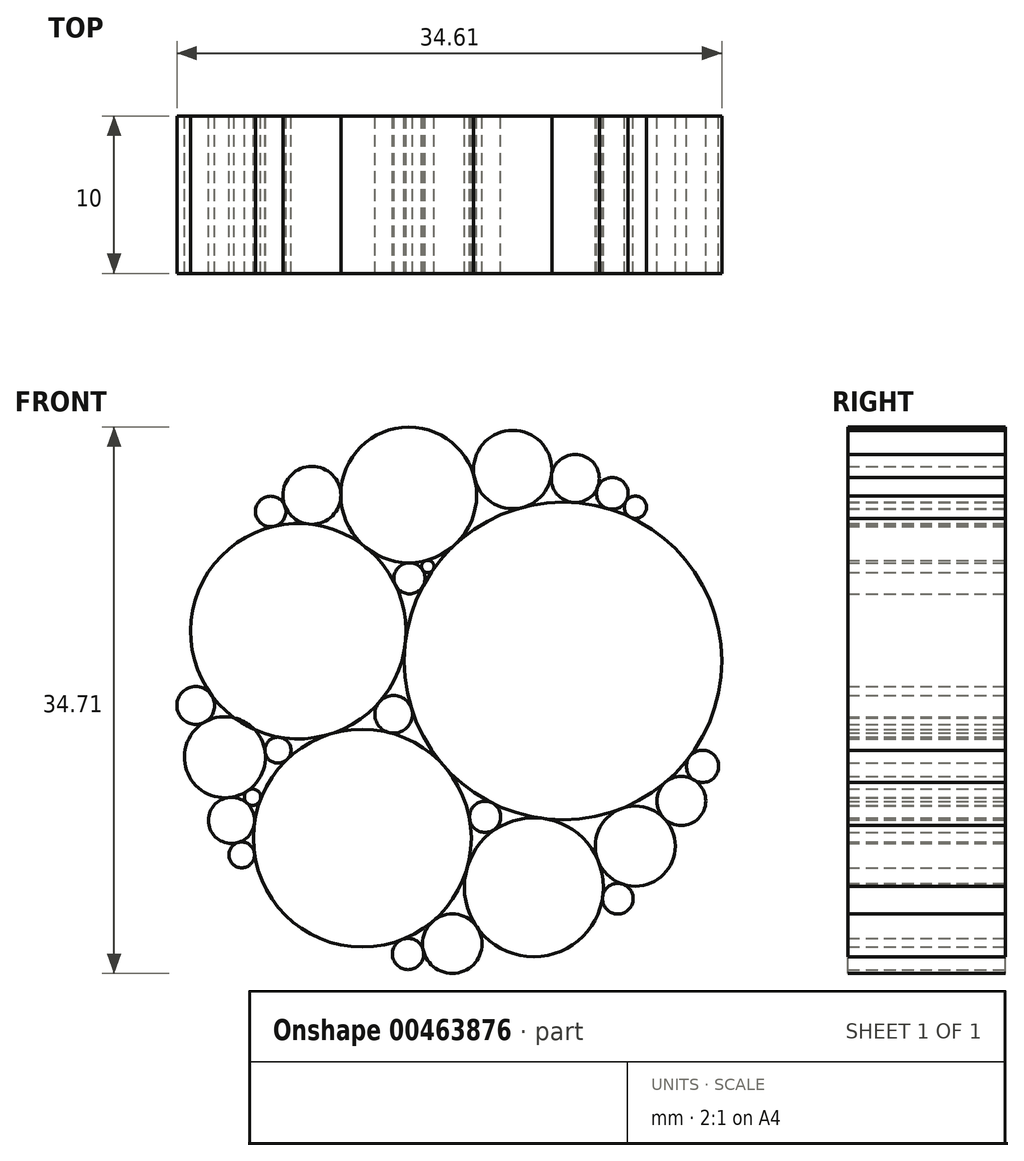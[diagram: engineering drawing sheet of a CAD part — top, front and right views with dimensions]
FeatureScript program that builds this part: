
annotation { "Feature Type Name" : "Feature", "Feature Type Description" : "" }
export const myFeature = defineFeature(function(context is Context, id is Id, definition is map)
    precondition{}
    {
        {
            var Q0;
            Q0=qCreatedBy(makeId("Front.planeOp"),FACE);
            var sketch = newSketch(context, id + "F0", { "sketchPlane" : qUnion([Q0])});
            skCircle(sketch, "E0", {"center": v(0, 0) * mm, "radius": 17.5 * mm});
            skCircle(sketch, "E1", {"center": v(-2.77, 12.9) * mm, "radius": 4.31 * mm});
            skPoint(sketch, "E1.first.point", {"position": v(-3.67, 17.11) * mm});
            skPoint(sketch, "E1.second.point", {"position": v(-3.67, 17.11) * mm});
            skPoint(sketch, "E1.third.point", {"position": v(-2.48, 8.6) * mm});
            skCircle(sketch, "E2", {"center": v(-5.71, -8.9) * mm, "radius": 6.92 * mm});
            skPoint(sketch, "E2.first.point", {"position": v(-9.45, -14.73) * mm});
            skPoint(sketch, "E2.second.point", {"position": v(-9.45, -14.73) * mm});
            skPoint(sketch, "E2.third.point", {"position": v(-1.47, -3.44) * mm});
            skCircle(sketch, "E3", {"center": v(-8.92, 12.87) * mm, "radius": 1.84 * mm});
            skPoint(sketch, "E3.first.point", {"position": v(-9.97, 14.38) * mm});
            skPoint(sketch, "E3.second.point", {"position": v(-9.97, 14.38) * mm});
            skPoint(sketch, "E3.third.point", {"position": v(-7.42, 11.8) * mm});
            skCircle(sketch, "E4", {"center": v(-1.56, 8.35) * mm, "radius": 0.4 * mm});
            skPoint(sketch, "E4.first.point", {"position": v(-1.66, 8.73) * mm});
            skPoint(sketch, "E4.second.point", {"position": v(-1.66, 8.73) * mm});
            skPoint(sketch, "E4.third.point", {"position": v(-1.33, 8.03) * mm});
            skCircle(sketch, "E5", {"center": v(3.84, 14.51) * mm, "radius": 2.49 * mm});
            skPoint(sketch, "E5.first.point", {"position": v(1.42, 13.92) * mm});
            skPoint(sketch, "E5.second.point", {"position": v(4.47, 16.92) * mm});
            skPoint(sketch, "E5.third.point", {"position": v(5.7, 12.86) * mm});
            skCircle(sketch, "E6", {"center": v(0, -15.61) * mm, "radius": 1.89 * mm});
            skPoint(sketch, "E6.first.point", {"position": v(0, -17.5) * mm});
            skPoint(sketch, "E6.second.point", {"position": v(0, -17.5) * mm});
            skPoint(sketch, "E6.third.point", {"position": v(-0.04, -13.72) * mm});
            skCircle(sketch, "E7", {"center": v(-9.79, 4.24) * mm, "radius": 6.84 * mm});
            skPoint(sketch, "E7.first.point", {"position": v(-16.06, 6.95) * mm});
            skPoint(sketch, "E7.second.point", {"position": v(-16.06, 6.95) * mm});
            skPoint(sketch, "E7.third.point", {"position": v(-2.95, 4.31) * mm});
            skCircle(sketch, "E8", {"center": v(-14.45, -3.77) * mm, "radius": 2.57 * mm});
            skPoint(sketch, "E8.first.point", {"position": v(-16.93, -4.41) * mm});
            skPoint(sketch, "E8.second.point", {"position": v(-16.93, -4.41) * mm});
            skPoint(sketch, "E8.third.point", {"position": v(-13.85, -1.26) * mm});
            skCircle(sketch, "E9", {"center": v(-14.02, -7.78) * mm, "radius": 1.46 * mm});
            skPoint(sketch, "E9.first.point", {"position": v(-15.3, -8.5) * mm});
            skPoint(sketch, "E9.second.point", {"position": v(-15.3, -8.5) * mm});
            skPoint(sketch, "E9.third.point", {"position": v(-12.57, -7.98) * mm});
            skCircle(sketch, "E10", {"center": v(-2.72, 7.6) * mm, "radius": 0.99 * mm});
            skPoint(sketch, "E10.first.point", {"position": v(-3.61, 7.17) * mm});
            skPoint(sketch, "E10.second.point", {"position": v(-2.73, 8.59) * mm});
            skPoint(sketch, "E10.third.point", {"position": v(-1.85, 7.13) * mm});
            skCircle(sketch, "E11", {"center": v(-3.73, -1.04) * mm, "radius": 1.2 * mm});
            skPoint(sketch, "E11.first.point", {"position": v(-4.63, -0.25) * mm});
            skPoint(sketch, "E11.second.point", {"position": v(-4.02, -2.2) * mm});
            skPoint(sketch, "E11.third.point", {"position": v(-2.56, -1.3) * mm});
            skCircle(sketch, "E12", {"center": v(-11.53, 11.84) * mm, "radius": 0.97 * mm});
            skPoint(sketch, "E12.first.point", {"position": v(-12.2, 12.54) * mm});
            skPoint(sketch, "E12.second.point", {"position": v(-12.2, 12.54) * mm});
            skPoint(sketch, "E12.third.point", {"position": v(-11.32, 10.9) * mm});
            skCircle(sketch, "E13", {"center": v(-11.08, -3.32) * mm, "radius": 0.83 * mm});
            skPoint(sketch, "E13.first.point", {"position": v(-11.9, -3.43) * mm});
            skPoint(sketch, "E13.second.point", {"position": v(-10.94, -2.5) * mm});
            skPoint(sketch, "E13.third.point", {"position": v(-10.5, -3.91) * mm});
            skCircle(sketch, "E14", {"center": v(7.03, 2.35) * mm, "radius": 10.09 * mm});
            skPoint(sketch, "E14.first.point", {"position": v(16.6, 5.55) * mm});
            skPoint(sketch, "E14.second.point", {"position": v(16.6, 5.55) * mm});
            skCircle(sketch, "E15", {"center": v(2.08, -7.55) * mm, "radius": 0.99 * mm});
            skPoint(sketch, "E15.first.point", {"position": v(1.1, -7.72) * mm});
            skPoint(sketch, "E15.second.point", {"position": v(2.52, -6.67) * mm});
            skPoint(sketch, "E15.third.point", {"position": v(2.5, -8.45) * mm});
            skCircle(sketch, "E16", {"center": v(-2.8, -16.27) * mm, "radius": 1 * mm});
            skPoint(sketch, "E16.first.point", {"position": v(-2.98, -17.24) * mm});
            skPoint(sketch, "E16.second.point", {"position": v(-2.98, -17.24) * mm});
            skPoint(sketch, "E16.third.point", {"position": v(-1.84, -16.04) * mm});
            skCircle(sketch, "E17", {"center": v(-16.3, -0.48) * mm, "radius": 1.2 * mm});
            skPoint(sketch, "E17.first.point", {"position": v(-17.5, -0.51) * mm});
            skPoint(sketch, "E17.second.point", {"position": v(-15.32, 0.22) * mm});
            skPoint(sketch, "E17.third.point", {"position": v(-15.7, -1.52) * mm});
            skCircle(sketch, "E18", {"center": v(-12.69, -6.31) * mm, "radius": 0.52 * mm});
            skPoint(sketch, "E18.first.point", {"position": v(-12.98, -5.88) * mm});
            skPoint(sketch, "E18.second.point", {"position": v(-13.04, -6.7) * mm});
            skPoint(sketch, "E18.third.point", {"position": v(-12.2, -6.5) * mm});
            skPoint(sketch, "E19.first.point", {"position": v(-1.92, 17.12) * mm});
            skPoint(sketch, "E19.second.point", {"position": v(3.48, 16.98) * mm});
            skPoint(sketch, "E19.third.point", {"position": v(3.95, 17.05) * mm});
            skCircle(sketch, "E20", {"center": v(7.8, 13.94) * mm, "radius": 1.53 * mm});
            skPoint(sketch, "E20.first.point", {"position": v(6.3, 14.15) * mm});
            skPoint(sketch, "E20.second.point", {"position": v(8.56, 15.27) * mm});
            skPoint(sketch, "E20.third.point", {"position": v(7.7, 12.41) * mm});
            skCircle(sketch, "E21", {"center": v(10.16, 13) * mm, "radius": 1 * mm});
            skPoint(sketch, "E21.first.point", {"position": v(9.23, 13.37) * mm});
            skPoint(sketch, "E21.second.point", {"position": v(10.78, 13.79) * mm});
            skPoint(sketch, "E21.third.point", {"position": v(9.88, 12.03) * mm});
            skCircle(sketch, "E22", {"center": v(5.18, -12.02) * mm, "radius": 4.4 * mm});
            skPoint(sketch, "E22.first.point", {"position": v(1.22, -10.08) * mm});
            skPoint(sketch, "E22.second.point", {"position": v(6.92, -16.07) * mm});
            skPoint(sketch, "E22.third.point", {"position": v(5.74, -7.65) * mm});
            skCircle(sketch, "E23", {"center": v(11.62, -9.41) * mm, "radius": 2.54 * mm});
            skPoint(sketch, "E23.first.point", {"position": v(9.26, -10.37) * mm});
            skPoint(sketch, "E23.second.point", {"position": v(13.6, -11.01) * mm});
            skPoint(sketch, "E23.third.point", {"position": v(13.94, -8.36) * mm});
            skCircle(sketch, "E24", {"center": v(14.54, -6.54) * mm, "radius": 1.55 * mm});
            skPoint(sketch, "E24.first.point", {"position": v(13.54, -5.35) * mm});
            skPoint(sketch, "E24.second.point", {"position": v(13.52, -7.71) * mm});
            skPoint(sketch, "E24.third.point", {"position": v(15.96, -7.18) * mm});
            skCircle(sketch, "E25", {"center": v(-13.38, -9.97) * mm, "radius": 0.82 * mm});
            skPoint(sketch, "E25.first.point", {"position": v(-14.03, -10.46) * mm});
            skPoint(sketch, "E25.second.point", {"position": v(-12.57, -9.86) * mm});
            skPoint(sketch, "E25.third.point", {"position": v(-13.6, -9.18) * mm});
            skCircle(sketch, "E26", {"center": v(15.9, -4.35) * mm, "radius": 1.02 * mm});
            skPoint(sketch, "E26.first.point", {"position": v(15.36, -5.22) * mm});
            skPoint(sketch, "E26.second.point", {"position": v(15.6, -3.36) * mm});
            skPoint(sketch, "E26.third.point", {"position": v(16.52, -3.54) * mm});
            skCircle(sketch, "E27", {"center": v(11.63, 12.11) * mm, "radius": 0.7 * mm});
            skPoint(sketch, "E27.first.point", {"position": v(12.12, 12.62) * mm});
            skPoint(sketch, "E27.second.point", {"position": v(11.02, 12.48) * mm});
            skPoint(sketch, "E27.third.point", {"position": v(11.33, 11.48) * mm});
            skCircle(sketch, "E28", {"center": v(10.51, -12.75) * mm, "radius": 0.97 * mm});
            skPoint(sketch, "E28.first.point", {"position": v(9.55, -12.62) * mm});
            skPoint(sketch, "E28.second.point", {"position": v(10.82, -11.83) * mm});
            skPoint(sketch, "E28.third.point", {"position": v(11.13, -13.5) * mm});
            skSolve(sketch);
        }
        {
            var Q0;
            {var subQ0=sQuery(id+"F0.wireOp",EDGE,"E12");var subQ1=makeQuery(id+"F0.imprint","INTERSECT",VERTEX,{"derivedFrom":[sQuery(id+"F0.wireOp",EDGE,"E0"),subQ0]});Q0=makeQuery(id+"F0.imprint","IMPRINT",FACE,{"disambiguationData":[TD([[makeQuery(id+"F0.imprint","IMPRINT",EDGE,{"disambiguationData":[TD([[subQ1,1.0]])],"derivedFrom":subQ0}),1.0]])]});}
            var Q1;
            {var subQ0=sQuery(id+"F0.wireOp",EDGE,"E16");var subQ1=makeQuery(id+"F0.imprint","INTERSECT",VERTEX,{"derivedFrom":[sQuery(id+"F0.wireOp",EDGE,"E2"),subQ0]});Q1=makeQuery(id+"F0.imprint","IMPRINT",FACE,{"disambiguationData":[TD([[makeQuery(id+"F0.imprint","IMPRINT",EDGE,{"disambiguationData":[TD([[subQ1,1.0]])],"derivedFrom":subQ0}),1.0]])]});}
            var Q2;
            {var subQ0=sQuery(id+"F0.wireOp",EDGE,"E17");var subQ1=makeQuery(id+"F0.imprint","INTERSECT",VERTEX,{"derivedFrom":[sQuery(id+"F0.wireOp",EDGE,"E0"),subQ0]});Q2=makeQuery(id+"F0.imprint","IMPRINT",FACE,{"disambiguationData":[TD([[makeQuery(id+"F0.imprint","IMPRINT",EDGE,{"disambiguationData":[TD([[subQ1,1.0]])],"derivedFrom":subQ0}),1.0]])]});}
            var Q3;
            {var subQ0=sQuery(id+"F0.wireOp",EDGE,"E25");var subQ1=makeQuery(id+"F0.imprint","INTERSECT",VERTEX,{"derivedFrom":[sQuery(id+"F0.wireOp",EDGE,"E2"),subQ0]});Q3=makeQuery(id+"F0.imprint","IMPRINT",FACE,{"disambiguationData":[TD([[makeQuery(id+"F0.imprint","IMPRINT",EDGE,{"disambiguationData":[TD([[subQ1,-1.0]])],"derivedFrom":subQ0}),1.0]])]});}
            var Q4;
            {var subQ0=sQuery(id+"F0.wireOp",EDGE,"E26");var subQ1=makeQuery(id+"F0.imprint","INTERSECT",VERTEX,{"derivedFrom":[sQuery(id+"F0.wireOp",EDGE,"E14"),subQ0]});Q4=makeQuery(id+"F0.imprint","IMPRINT",FACE,{"disambiguationData":[TD([[makeQuery(id+"F0.imprint","IMPRINT",EDGE,{"disambiguationData":[TD([[subQ1,-1.0]])],"derivedFrom":subQ0}),1.0]])]});}
            var Q5;
            {var subQ0=sQuery(id+"F0.wireOp",EDGE,"E27");var subQ1=makeQuery(id+"F0.imprint","INTERSECT",VERTEX,{"derivedFrom":[sQuery(id+"F0.wireOp",EDGE,"E0"),subQ0]});Q5=makeQuery(id+"F0.imprint","IMPRINT",FACE,{"disambiguationData":[TD([[makeQuery(id+"F0.imprint","IMPRINT",EDGE,{"disambiguationData":[TD([[subQ1,-1.0]])],"derivedFrom":subQ0}),1.0]])]});}
            var Q6;
            {var subQ0=sQuery(id+"F0.wireOp",EDGE,"E28");var subQ1=makeQuery(id+"F0.imprint","INTERSECT",VERTEX,{"derivedFrom":[sQuery(id+"F0.wireOp",EDGE,"E22"),subQ0]});Q6=makeQuery(id+"F0.imprint","IMPRINT",FACE,{"disambiguationData":[TD([[makeQuery(id+"F0.imprint","IMPRINT",EDGE,{"disambiguationData":[TD([[subQ1,1.0]])],"derivedFrom":subQ0}),1.0]])]});}
            var Q7;
            {var subQ0=sQuery(id+"F0.wireOp",EDGE,"E5");var subQ1=makeQuery(id+"F0.imprint","INTERSECT",VERTEX,{"derivedFrom":[sQuery(id+"F0.wireOp",EDGE,"E0"),subQ0]});Q7=makeQuery(id+"F0.imprint","IMPRINT",FACE,{"disambiguationData":[TD([[makeQuery(id+"F0.imprint","IMPRINT",EDGE,{"disambiguationData":[TD([[subQ1,-1.0]])],"derivedFrom":subQ0}),1.0]])]});}
            var Q8;
            {var subQ0=sQuery(id+"F0.wireOp",EDGE,"E6");var subQ1=makeQuery(id+"F0.imprint","INTERSECT",VERTEX,{"derivedFrom":[sQuery(id+"F0.wireOp",EDGE,"E2"),subQ0]});Q8=makeQuery(id+"F0.imprint","IMPRINT",FACE,{"disambiguationData":[TD([[makeQuery(id+"F0.imprint","IMPRINT",EDGE,{"disambiguationData":[TD([[subQ1,1.0]])],"derivedFrom":subQ0}),1.0]])]});}
            var Q9;
            {var subQ0=sQuery(id+"F0.wireOp",EDGE,"E20");var subQ1=makeQuery(id+"F0.imprint","INTERSECT",VERTEX,{"derivedFrom":[sQuery(id+"F0.wireOp",EDGE,"E0"),subQ0]});Q9=makeQuery(id+"F0.imprint","IMPRINT",FACE,{"disambiguationData":[TD([[makeQuery(id+"F0.imprint","IMPRINT",EDGE,{"disambiguationData":[TD([[subQ1,-1.0]])],"derivedFrom":subQ0}),1.0]])]});}
            var Q10;
            {var subQ0=sQuery(id+"F0.wireOp",EDGE,"E21");var subQ1=makeQuery(id+"F0.imprint","INTERSECT",VERTEX,{"derivedFrom":[sQuery(id+"F0.wireOp",EDGE,"E0"),subQ0]});Q10=makeQuery(id+"F0.imprint","IMPRINT",FACE,{"disambiguationData":[TD([[makeQuery(id+"F0.imprint","IMPRINT",EDGE,{"disambiguationData":[TD([[subQ1,-1.0]])],"derivedFrom":subQ0}),1.0]])]});}
            var Q11;
            {var subQ0=sQuery(id+"F0.wireOp",EDGE,"E24");var subQ1=makeQuery(id+"F0.imprint","INTERSECT",VERTEX,{"derivedFrom":[sQuery(id+"F0.wireOp",EDGE,"E14"),subQ0]});Q11=makeQuery(id+"F0.imprint","IMPRINT",FACE,{"disambiguationData":[TD([[makeQuery(id+"F0.imprint","IMPRINT",EDGE,{"disambiguationData":[TD([[subQ1,1.0]])],"derivedFrom":subQ0}),1.0]])]});}
            var Q12;
            {var subQ0=sQuery(id+"F0.wireOp",EDGE,"E3");var subQ4=sQuery(id+"F0.wireOp",EDGE,"E1");var subQ5=makeQuery(id+"F0.imprint","INTERSECT",VERTEX,{"disambiguationData":[OD(0.0)],"derivedFrom":[subQ4,subQ0]});Q12=makeQuery(id+"F0.imprint","IMPRINT",FACE,{"disambiguationData":[TD([[makeQuery(id+"F0.imprint","IMPRINT",EDGE,{"disambiguationData":[TD([[subQ5,1.0]])],"derivedFrom":subQ0}),1.0]])]});}
            var Q13;
            {var subQ0=sQuery(id+"F0.wireOp",EDGE,"E9");var subQ4=makeQuery(id+"F0.imprint","INTERSECT",VERTEX,{"derivedFrom":[sQuery(id+"F0.wireOp",EDGE,"E8"),subQ0]});Q13=makeQuery(id+"F0.imprint","IMPRINT",FACE,{"disambiguationData":[TD([[makeQuery(id+"F0.imprint","IMPRINT",EDGE,{"disambiguationData":[TD([[subQ4,1.0]])],"derivedFrom":subQ0}),1.0]])]});}
            var Q14;
            {var subQ0=sQuery(id+"F0.wireOp",EDGE,"E23");var subQ4=makeQuery(id+"F0.imprint","INTERSECT",VERTEX,{"derivedFrom":[sQuery(id+"F0.wireOp",EDGE,"E14"),subQ0]});Q14=makeQuery(id+"F0.imprint","IMPRINT",FACE,{"disambiguationData":[TD([[makeQuery(id+"F0.imprint","IMPRINT",EDGE,{"disambiguationData":[TD([[subQ4,1.0]])],"derivedFrom":subQ0}),1.0]])]});}
            var Q15;
            {var subQ0=sQuery(id+"F0.wireOp",EDGE,"E22");var subQ4=makeQuery(id+"F0.imprint","INTERSECT",VERTEX,{"derivedFrom":[sQuery(id+"F0.wireOp",EDGE,"E14"),subQ0]});Q15=makeQuery(id+"F0.imprint","IMPRINT",FACE,{"disambiguationData":[TD([[makeQuery(id+"F0.imprint","IMPRINT",EDGE,{"disambiguationData":[TD([[subQ4,1.0]])],"derivedFrom":subQ0}),1.0]])]});}
            var Q16;
            {var subQ0=sQuery(id+"F0.wireOp",EDGE,"E8");var subQ3=sQuery(id+"F0.wireOp",EDGE,"E7");var subQ4=makeQuery(id+"F0.imprint","INTERSECT",VERTEX,{"disambiguationData":[OD(0.0)],"derivedFrom":[subQ3,subQ0]});Q16=makeQuery(id+"F0.imprint","IMPRINT",FACE,{"disambiguationData":[TD([[makeQuery(id+"F0.imprint","IMPRINT",EDGE,{"disambiguationData":[TD([[subQ4,-1.0]])],"derivedFrom":subQ3}),-1.0]])]});}
            var Q17;
            {var subQ0=sQuery(id+"F0.wireOp",EDGE,"E1");var subQ5=makeQuery(id+"F0.imprint","INTERSECT",VERTEX,{"derivedFrom":[sQuery(id+"F0.wireOp",EDGE,"E0"),subQ0]});Q17=makeQuery(id+"F0.imprint","IMPRINT",FACE,{"disambiguationData":[TD([[makeQuery(id+"F0.imprint","IMPRINT",EDGE,{"disambiguationData":[TD([[subQ5,1.0]])],"derivedFrom":subQ0}),1.0]])]});}
            var Q18;
            {var subQ0=sQuery(id+"F0.wireOp",EDGE,"E2");var subQ8=makeQuery(id+"F0.imprint","INTERSECT",VERTEX,{"derivedFrom":[subQ0,sQuery(id+"F0.wireOp",EDGE,"E14")]});Q18=makeQuery(id+"F0.imprint","IMPRINT",FACE,{"disambiguationData":[TD([[makeQuery(id+"F0.imprint","IMPRINT",EDGE,{"disambiguationData":[TD([[subQ8,1.0]])],"derivedFrom":subQ0}),1.0]])]});}
            var Q19;
            {var subQ0=sQuery(id+"F0.wireOp",EDGE,"E7");var subQ10=makeQuery(id+"F0.imprint","INTERSECT",VERTEX,{"derivedFrom":[sQuery(id+"F0.wireOp",EDGE,"E1"),subQ0]});Q19=makeQuery(id+"F0.imprint","IMPRINT",FACE,{"disambiguationData":[TD([[makeQuery(id+"F0.imprint","IMPRINT",EDGE,{"disambiguationData":[TD([[subQ10,1.0]])],"derivedFrom":subQ0}),1.0]])]});}
            var Q20;
            {var subQ0=sQuery(id+"F0.wireOp",EDGE,"E14");var subQ8=makeQuery(id+"F0.imprint","INTERSECT",VERTEX,{"derivedFrom":[sQuery(id+"F0.wireOp",EDGE,"E0"),subQ0]});Q20=makeQuery(id+"F0.imprint","IMPRINT",FACE,{"disambiguationData":[TD([[makeQuery(id+"F0.imprint","IMPRINT",EDGE,{"disambiguationData":[TD([[subQ8,-1.0]])],"derivedFrom":subQ0}),1.0]])]});}
            var Q21;
            {var subQ0=sQuery(id+"F0.wireOp",EDGE,"E11");var subQ1=makeQuery(id+"F0.imprint","INTERSECT",VERTEX,{"derivedFrom":[sQuery(id+"F0.wireOp",EDGE,"E7"),subQ0]});Q21=makeQuery(id+"F0.imprint","IMPRINT",FACE,{"disambiguationData":[TD([[makeQuery(id+"F0.imprint","IMPRINT",EDGE,{"disambiguationData":[TD([[subQ1,1.0]])],"derivedFrom":subQ0}),1.0]])]});}
            var Q22;
            {var subQ0=sQuery(id+"F0.wireOp",EDGE,"E13");var subQ1=makeQuery(id+"F0.imprint","INTERSECT",VERTEX,{"derivedFrom":[sQuery(id+"F0.wireOp",EDGE,"E7"),subQ0]});Q22=makeQuery(id+"F0.imprint","IMPRINT",FACE,{"disambiguationData":[TD([[makeQuery(id+"F0.imprint","IMPRINT",EDGE,{"disambiguationData":[TD([[subQ1,-1.0]])],"derivedFrom":subQ0}),1.0]])]});}
            var Q23;
            {var subQ0=sQuery(id+"F0.wireOp",EDGE,"E18");var subQ1=makeQuery(id+"F0.imprint","INTERSECT",VERTEX,{"derivedFrom":[sQuery(id+"F0.wireOp",EDGE,"E8"),subQ0]});Q23=makeQuery(id+"F0.imprint","IMPRINT",FACE,{"disambiguationData":[TD([[makeQuery(id+"F0.imprint","IMPRINT",EDGE,{"disambiguationData":[TD([[subQ1,-1.0]])],"derivedFrom":subQ0}),1.0]])]});}
            var Q24;
            {var subQ0=sQuery(id+"F0.wireOp",EDGE,"E10");var subQ1=makeQuery(id+"F0.imprint","INTERSECT",VERTEX,{"derivedFrom":[sQuery(id+"F0.wireOp",EDGE,"E1"),subQ0]});Q24=makeQuery(id+"F0.imprint","IMPRINT",FACE,{"disambiguationData":[TD([[makeQuery(id+"F0.imprint","IMPRINT",EDGE,{"disambiguationData":[TD([[subQ1,1.0]])],"derivedFrom":subQ0}),1.0]])]});}
            var Q25;
            {var subQ0=sQuery(id+"F0.wireOp",EDGE,"E4");var subQ1=makeQuery(id+"F0.imprint","INTERSECT",VERTEX,{"derivedFrom":[sQuery(id+"F0.wireOp",EDGE,"E1"),subQ0]});Q25=makeQuery(id+"F0.imprint","IMPRINT",FACE,{"disambiguationData":[TD([[makeQuery(id+"F0.imprint","IMPRINT",EDGE,{"disambiguationData":[TD([[subQ1,-1.0]])],"derivedFrom":subQ0}),1.0]])]});}
            var Q26;
            {var subQ0=sQuery(id+"F0.wireOp",EDGE,"E15");var subQ1=makeQuery(id+"F0.imprint","INTERSECT",VERTEX,{"derivedFrom":[sQuery(id+"F0.wireOp",EDGE,"E2"),subQ0]});Q26=makeQuery(id+"F0.imprint","IMPRINT",FACE,{"disambiguationData":[TD([[makeQuery(id+"F0.imprint","IMPRINT",EDGE,{"disambiguationData":[TD([[subQ1,1.0]])],"derivedFrom":subQ0}),1.0]])]});}
            extrude(context, id + "F1", {"entities" : qUnion([Q0, Q1, Q2, Q3, Q4, Q5, Q6, Q7, Q8, Q9, Q10, Q11, Q12, Q13, Q14, Q15, Q16, Q17, Q18, Q19, Q20, Q21, Q22, Q23, Q24, Q25, Q26]), "depth" : 10 * mm});
        }
    });
